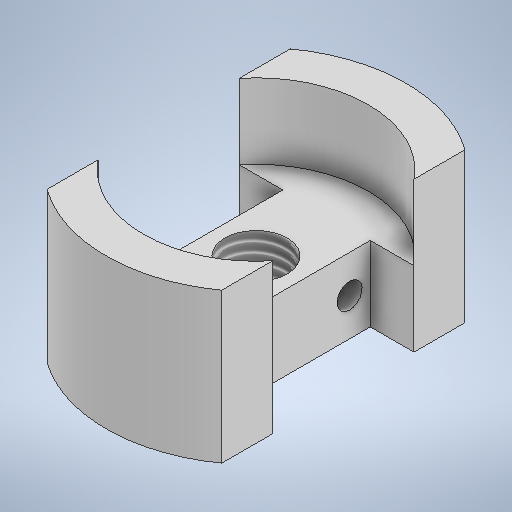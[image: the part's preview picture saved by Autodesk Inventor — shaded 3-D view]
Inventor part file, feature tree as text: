
AUTODESK INVENTOR PART (.ipt)
format: ipt  version: 2025.1 (Build 291241000, 241)  size: 313,344 bytes
history: native  units: mm
features: sketch x3, extrude x3, thread x1, hole x1
ambient origin geometry x8: Origin, YZ Plane, XZ Plane, XY Plane, X Axis, Y Axis, Z Axis, Center Point
bodies: Solid1 (feature_tree)
feature tree (8):
  sketch  "Sketch1"  dims[d4=24.0mm d5=12.0mm]
  extrude  "Extrusion1"  Depth=12.0mm
  extrude  "Extrusion2"  Depth=9.0mm
  extrude  "Extrusion3"  Depth=12.0mm
  thread  "Thread1"  [1 undecoded]
  hole  "Hole1"  [1 undecoded]
  sketch  "Sketch2"  dims[d6=14.0mm d7=9.0mm]
  sketch  "Sketch3"  dims[d8=3.5mm d9=12.0mm d10=7.0mm d11=3.5mm d12=9.0mm d13=12.0mm d14=6.0mm d15=0.0mm d16=12.0mm d17=0.0mm d18=12.0mm d19=5.0mm d20=12.0mm d21=0.0mm d22=6.0mm d23=0.0mm d24=3.0mm d25=8.0mm d26=4.0mm d27=2.0mm d28=2.0mm d29=4.0mm d30=2.0mm d31=90.0deg d32=8.0mm d33=0.0mm]
note: 2 required parameter values undecoded (feature->parameter linkage not recoverable at this tier; creation-order binding heuristic only, values carry confidence <= 0.55)
